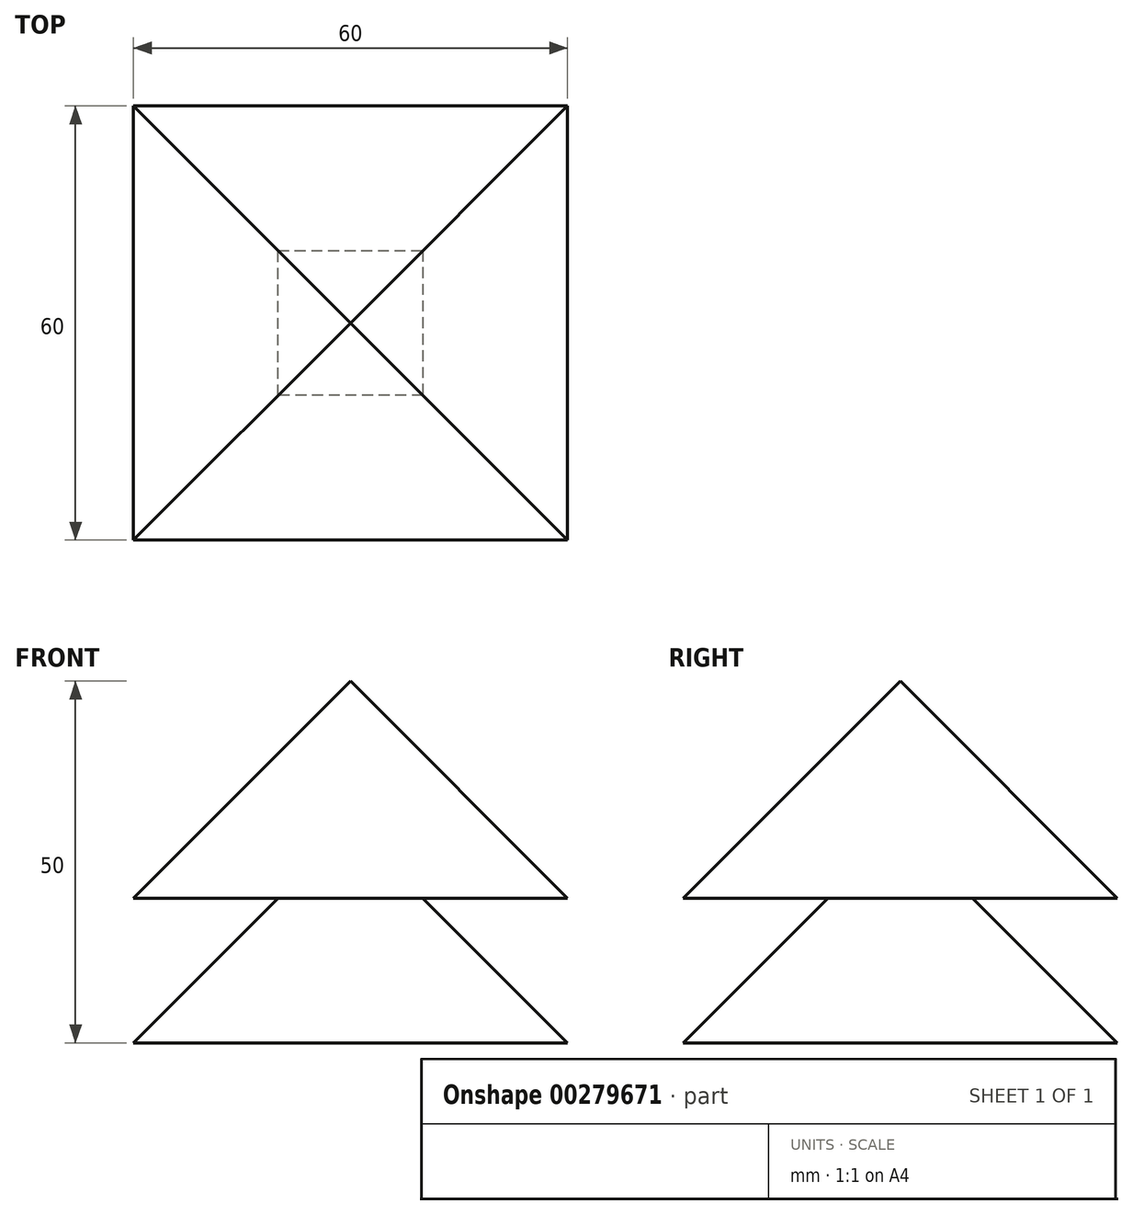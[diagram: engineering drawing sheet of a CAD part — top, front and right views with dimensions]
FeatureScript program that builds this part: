
annotation { "Feature Type Name" : "Feature", "Feature Type Description" : "" }
export const myFeature = defineFeature(function(context is Context, id is Id, definition is map)
    precondition{}
    {
        {
            var Q0;
            Q0=qCreatedBy(makeId("Top.planeOp"),FACE);
            var sketch = newSketch(context, id + "F0", { "sketchPlane" : qUnion([Q0])});
            skLineSegment(sketch, "E0.bottom", {"start": v(30, -30) * mm, "end": v(-30, -30) * mm});
            skLineSegment(sketch, "E0.top", {"start": v(30, 30) * mm, "end": v(-30, 30) * mm});
            skLineSegment(sketch, "E0.left", {"start": v(30, -30) * mm, "end": v(30, 30) * mm});
            skLineSegment(sketch, "E0.right", {"start": v(-30, -30) * mm, "end": v(-30, 30) * mm});
            skPoint(sketch, "E0.middle", {"position": v(0, 0) * mm});
            skSolve(sketch);
        }
        {
            var Q0;
            Q0 = qSketchRegion(id + "F0", true);
            extrude(context, id + "F1", {"entities" : qUnion([Q0]), "depth" : 30 * mm, "hasDraft" : true, "draftAngle" : 45 * degree, "draftPullDirection" : true});
        }
        {
            var Q0;
            Q0=qCreatedBy(makeId("Top.planeOp"),FACE);
            cPlane(context, id + "F2", {"entities" : qUnion([Q0]), "cplaneType" : CPlaneType.OFFSET, "offset" : 20 * mm, "width" : 150 * mm, "height" : 150 * mm});
        }
        {
            var Q0;
            Q0=qCreatedBy(id+"F2.planeOp",FACE);
            var sketch = newSketch(context, id + "F3", { "sketchPlane" : qUnion([Q0])});
            skLineSegment(sketch, "E1.0.0", {"start": v(-30, -30) * mm, "end": v(30, -30) * mm});
            skLineSegment(sketch, "E1.0.1", {"start": v(0, 0) * mm, "end": v(30, -30) * mm});
            skLineSegment(sketch, "E1.0.2", {"start": v(0, 0) * mm, "end": v(-30, -30) * mm});
            skLineSegment(sketch, "E2.0", {"start": v(30, -30) * mm, "end": v(30, 30) * mm});
            skLineSegment(sketch, "E3.0.1", {"start": v(30, 30) * mm, "end": v(0, 0) * mm});
            skLineSegment(sketch, "E4.0.0", {"start": v(30, 30) * mm, "end": v(-30, 30) * mm});
            skLineSegment(sketch, "E4.0.1", {"start": v(0, 0) * mm, "end": v(-30, 30) * mm});
            skLineSegment(sketch, "E4.0.2", {"start": v(0, 0) * mm, "end": v(30, 30) * mm});
            skLineSegment(sketch, "E5.0.0", {"start": v(-30, 30) * mm, "end": v(-30, -30) * mm});
            skLineSegment(sketch, "E5.0.1", {"start": v(-30, -30) * mm, "end": v(0, 0) * mm});
            skSolve(sketch);
        }
        {
            var Q0;
            Q0 = qSketchRegion(id + "F3", true);
            extrude(context, id + "F4", {"entities" : qUnion([Q0]), "operationType" : NewBodyOperationType.ADD, "depth" : 30 * mm, "hasDraft" : true, "draftAngle" : 45 * degree, "draftPullDirection" : true});
        }
    });
